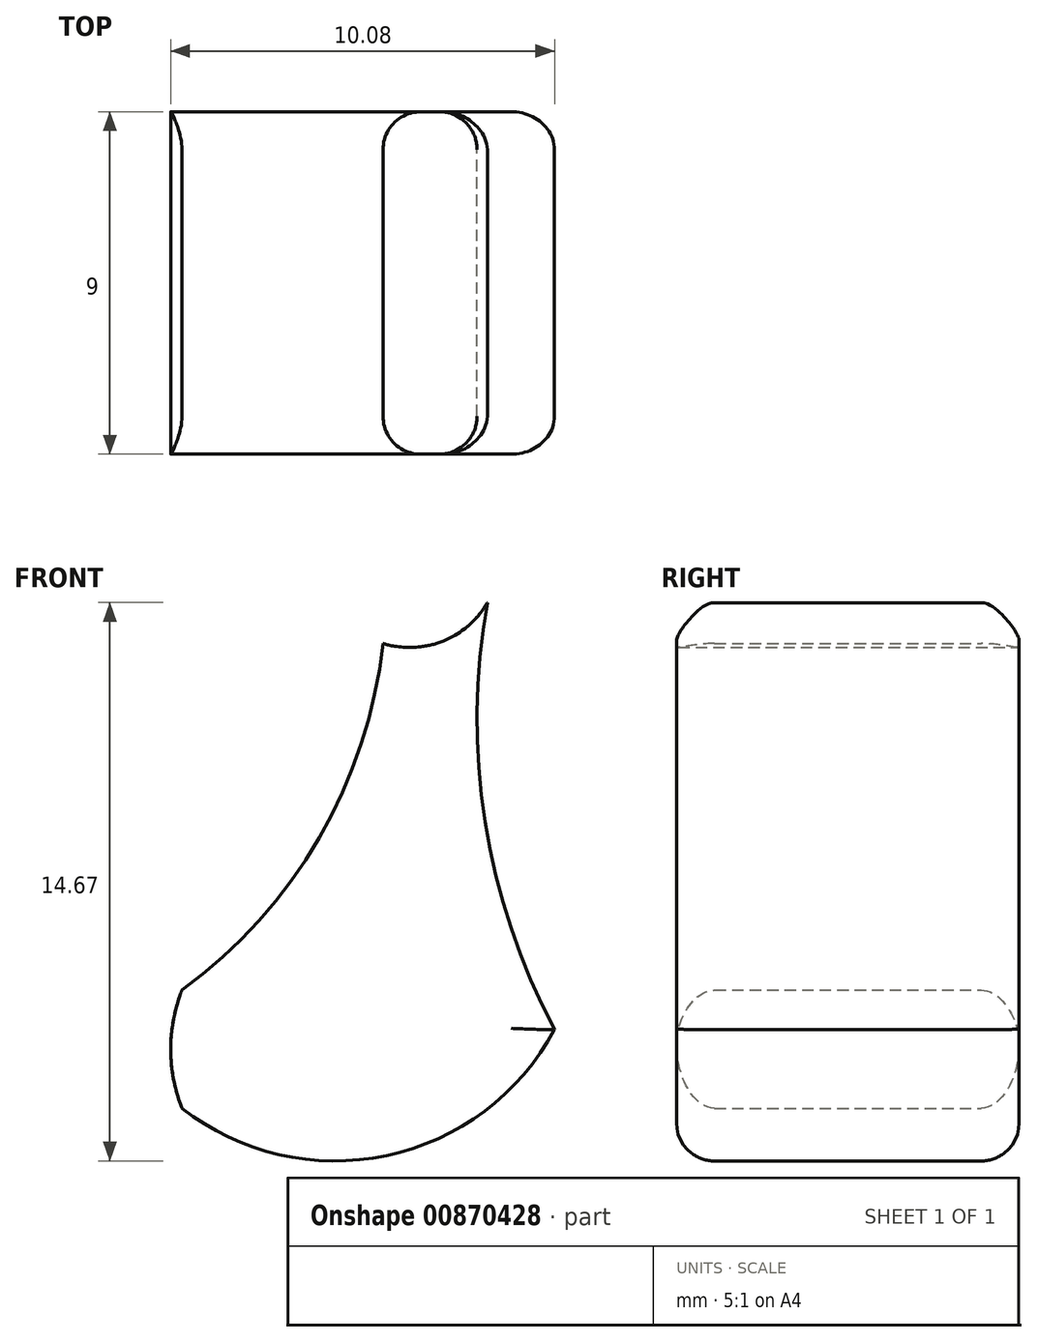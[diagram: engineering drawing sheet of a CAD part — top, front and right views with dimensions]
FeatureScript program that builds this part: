
annotation { "Feature Type Name" : "Feature", "Feature Type Description" : "" }
export const myFeature = defineFeature(function(context is Context, id is Id, definition is map)
    precondition{}
    {
        {
            var Q0;
            Q0=qCreatedBy(makeId("Front.planeOp"),FACE);
            var sketch = newSketch(context, id + "F0", { "sketchPlane" : qUnion([Q0])});
            skArc(sketch, "E0", {"start": v(13, 23.15) * mm, "mid": v(12.94, 17.4) * mm, "end": v(14.77, 11.93) * mm});
            skArc(sketch, "E1", {"start": v(4.98, 12.97) * mm, "mid": v(8.58, 16.96) * mm, "end": v(10.26, 22.08) * mm});
            skArc(sketch, "E2", {"start": v(4.98, 9.86) * mm, "mid": v(10.36, 8.62) * mm, "end": v(14.77, 11.93) * mm});
            skArc(sketch, "E3", {"start": v(4.98, 12.97) * mm, "mid": v(4.69, 11.41) * mm, "end": v(4.98, 9.86) * mm});
            skArc(sketch, "E4", {"start": v(10.26, 22.08) * mm, "mid": v(11.82, 22.13) * mm, "end": v(13, 23.15) * mm});
            skSolve(sketch);
        }
        {
            var Q0;
            Q0 = qSketchRegion(id + "F0", true);
            extrude(context, id + "F1", {"entities" : qUnion([Q0]), "depth" : 9 * mm, "offsetDistance" : 25 * mm});
        }
        {
            var Q0;
            Q0=makeQuery(id+"F1.opExtrude","CAP_EDGE",EDGE,{"disambiguationData":[OSD([sQuery(id+"F0.wireOp",EDGE,"E1")])],"isStart":false});
            var Q1;
            Q1=makeQuery(id+"F1.opExtrude","CAP_EDGE",EDGE,{"disambiguationData":[OSD([sQuery(id+"F0.wireOp",EDGE,"E0")])],"isStart":false});
            var Q2;
            Q2=makeQuery(id+"F1.opExtrude","CAP_EDGE",EDGE,{"disambiguationData":[OSD([sQuery(id+"F0.wireOp",EDGE,"E2")])],"isStart":false});
            fillet(context, id + "F2", {"entities" : qUnion([Q0, Q1, Q2]), "radius" : 1 * mm, "tangentPropagation" : true, "allowEdgeOverflow" : false});
        }
        {
            var Q0;
            Q0=makeQuery(id+"F1.opExtrude","CAP_EDGE",EDGE,{"disambiguationData":[OSD([sQuery(id+"F0.wireOp",EDGE,"E0")])],"isStart":true});
            var Q1;
            Q1=makeQuery(id+"F1.opExtrude","CAP_EDGE",EDGE,{"disambiguationData":[OSD([sQuery(id+"F0.wireOp",EDGE,"E2")])],"isStart":true});
            var Q2;
            Q2=makeQuery(id+"F1.opExtrude","CAP_EDGE",EDGE,{"disambiguationData":[OSD([sQuery(id+"F0.wireOp",EDGE,"E1")])],"isStart":true});
            fillet(context, id + "F3", {"entities" : qUnion([Q0, Q1, Q2]), "radius" : 1 * mm, "tangentPropagation" : true, "allowEdgeOverflow" : false});
        }
    });
